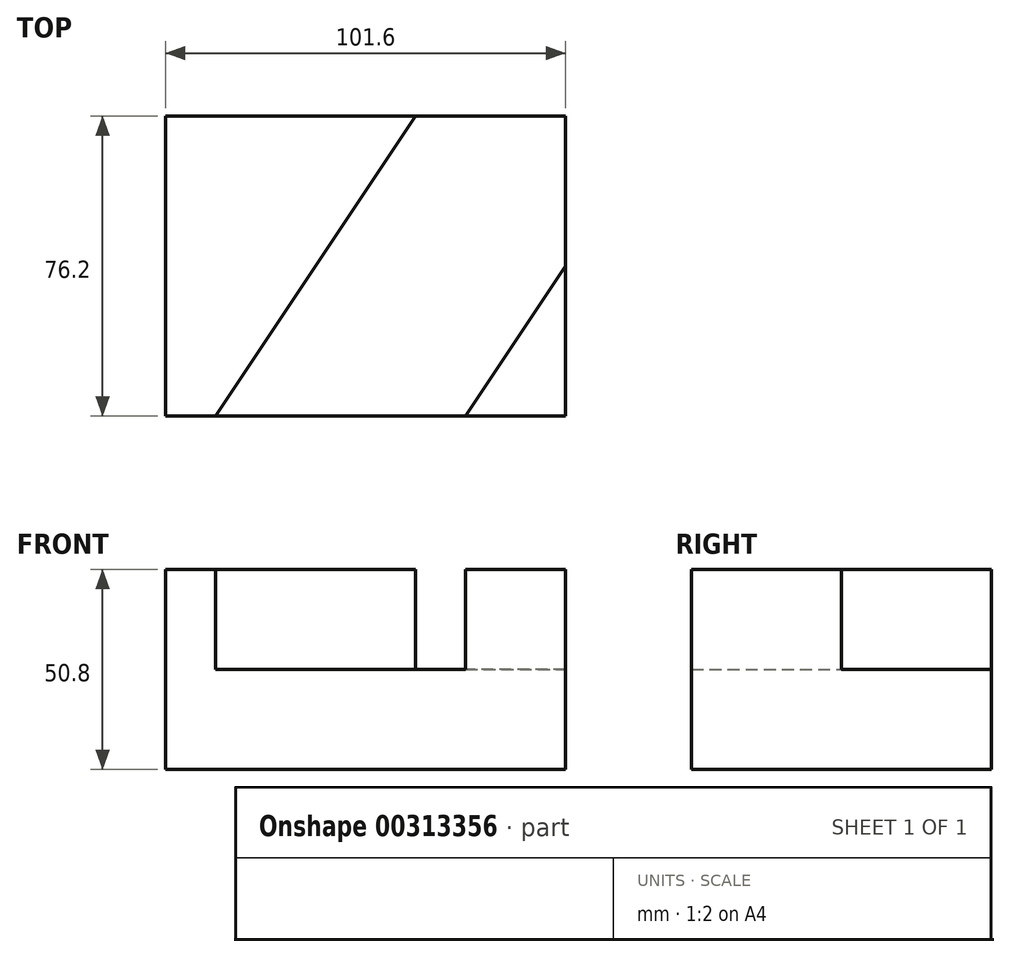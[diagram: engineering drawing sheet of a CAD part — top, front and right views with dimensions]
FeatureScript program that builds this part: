
annotation { "Feature Type Name" : "Feature", "Feature Type Description" : "" }
export const myFeature = defineFeature(function(context is Context, id is Id, definition is map)
    precondition{}
    {
        {
            var Q0;
            Q0=qCreatedBy(makeId("Front.planeOp"),FACE);
            var sketch = newSketch(context, id + "F0", { "sketchPlane" : qUnion([Q0])});
            skLineSegment(sketch, "E0", {"start": v(-48.15, -52.83) * mm, "end": v(53.45, -52.83) * mm});
            skLineSegment(sketch, "E1", {"start": v(53.45, -52.83) * mm, "end": v(53.45, -2.03) * mm});
            skLineSegment(sketch, "E2", {"start": v(53.45, -2.03) * mm, "end": v(-48.15, -2.03) * mm});
            skLineSegment(sketch, "E3", {"start": v(-48.15, -2.03) * mm, "end": v(-48.15, -52.83) * mm});
            skSolve(sketch);
        }
        {
            var Q0;
            Q0=makeQuery(id+"F0.imprint","IMPRINT",FACE,{"disambiguationData":[TD([[makeQuery(id+"F0.imprint","IMPRINT",EDGE,{"derivedFrom":sQuery(id+"F0.wireOp",EDGE,"E0")}),1.0]])]});
            extrude(context, id + "F1", {"entities" : qUnion([Q0]), "depth" : 76.2 * mm});
        }
        {
            var Q0;
            Q0=makeQuery(id+"F1.opExtrude","SWEPT_FACE",FACE,{"disambiguationData":[OSD([sQuery(id+"F0.wireOp",EDGE,"E2")])]});
            var sketch = newSketch(context, id + "F2", { "sketchPlane" : qUnion([Q0])});
            skLineSegment(sketch, "E4", {"start": v(28.05, -76.2) * mm, "end": v(53.45, -38.1) * mm});
            skLineSegment(sketch, "E5", {"start": v(53.45, -38.1) * mm, "end": v(53.45, -76.2) * mm});
            skLineSegment(sketch, "E6", {"start": v(53.45, -76.2) * mm, "end": v(28.05, -76.2) * mm});
            skLineSegment(sketch, "E7", {"start": v(-35.45, -76.2) * mm, "end": v(15.35, 0) * mm});
            skLineSegment(sketch, "E8", {"start": v(15.35, 0) * mm, "end": v(-48.15, 0) * mm});
            skLineSegment(sketch, "E9", {"start": v(-48.15, 0) * mm, "end": v(-48.15, -76.2) * mm});
            skLineSegment(sketch, "E10", {"start": v(-48.15, -76.2) * mm, "end": v(-35.45, -76.2) * mm});
            skSolve(sketch);
        }
        {
            var Q0;
            {var subQ4=sQuery(id+"F2.wireOp",EDGE,"E4");Q0=makeQuery(id+"F2.imprint","IMPRINT",FACE,{"disambiguationData":[TD([[makeQuery(id+"F2.imprint","IMPRINT",EDGE,{"derivedFrom":subQ4}),1.0]])]});}
            extrude(context, id + "F3", {"entities" : qUnion([Q0]), "operationType" : NewBodyOperationType.REMOVE, "oppositeDirection" : true, "depth" : 25.4 * mm});
        }
    });
